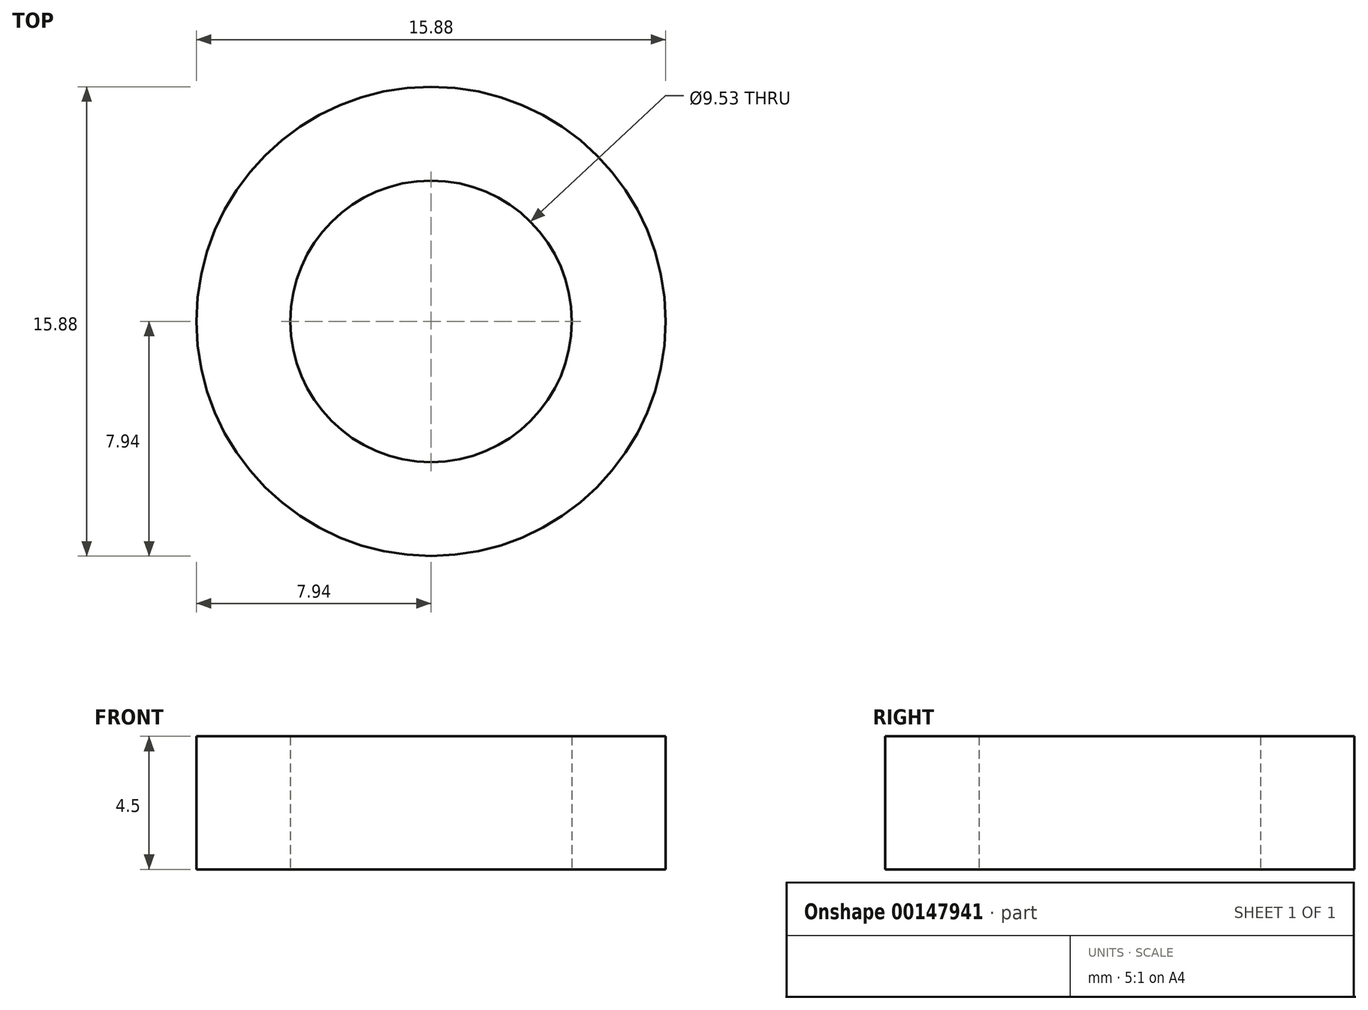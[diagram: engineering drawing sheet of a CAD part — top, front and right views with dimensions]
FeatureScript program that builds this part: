
annotation { "Feature Type Name" : "Feature", "Feature Type Description" : "" }
export const myFeature = defineFeature(function(context is Context, id is Id, definition is map)
    precondition{}
    {
        {
            var Q0;
            Q0=qCreatedBy(makeId("Top.planeOp"),FACE);
            var sketch = newSketch(context, id + "F0", { "sketchPlane" : qUnion([Q0])});
            skCircle(sketch, "E0", {"center": v(0, 0) * mm, "radius": 4.76 * mm});
            skCircle(sketch, "E1", {"center": v(0, 0) * mm, "radius": 7.94 * mm});
            skSolve(sketch);
        }
        {
            var Q0;
            Q0=qSketchRegion(id+"F0",true);
            extrude(context, id + "F1", {"entities" : qUnion([Q0]), "depth" : 4.5 * mm});
        }
    });
